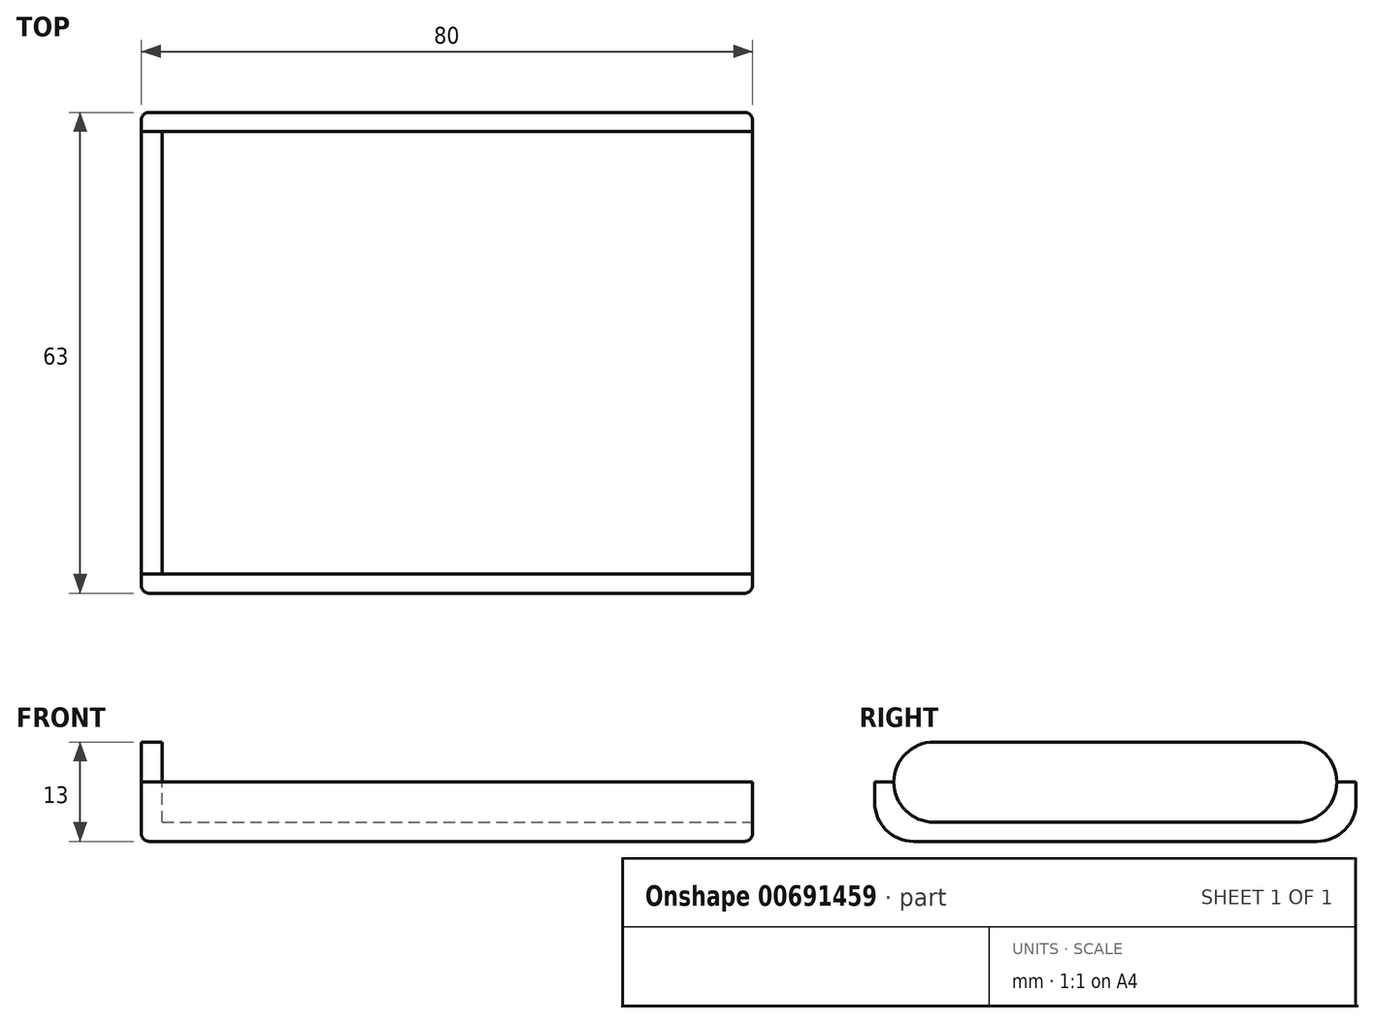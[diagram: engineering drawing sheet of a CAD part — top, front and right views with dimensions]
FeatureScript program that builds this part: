
annotation { "Feature Type Name" : "Feature", "Feature Type Description" : "" }
export const myFeature = defineFeature(function(context is Context, id is Id, definition is map)
    precondition{}
    {
        {
            var Q0;
            Q0=qCreatedBy(makeId("Top.planeOp"),FACE);
            var sketch = newSketch(context, id + "F0", { "sketchPlane" : qUnion([Q0])});
            skLineSegment(sketch, "E0.bottom", {"start": v(-31.63, 23.65) * mm, "end": v(48.37, 23.65) * mm});
            skLineSegment(sketch, "E0.top", {"start": v(-31.63, -39.35) * mm, "end": v(48.37, -39.35) * mm});
            skLineSegment(sketch, "E0.left", {"start": v(-31.63, 23.65) * mm, "end": v(-31.63, -39.35) * mm});
            skLineSegment(sketch, "E0.right", {"start": v(48.37, 23.65) * mm, "end": v(48.37, -39.35) * mm});
            skSolve(sketch);
        }
        {
            var Q0;
            Q0=makeQuery(id+"F0.imprint","IMPRINT",FACE,{"disambiguationData":[TD([[makeQuery(id+"F0.imprint","IMPRINT",EDGE,{"derivedFrom":sQuery(id+"F0.wireOp",EDGE,"E0.bottom")}),-1.0]])]});
            extrude(context, id + "F1", {"entities" : qUnion([Q0]), "depth" : 15.5 * mm, "offsetDistance" : 25.4 * mm});
        }
        {
            var Q0;
            Q0=makeQuery(id+"F1.opExtrude","SWEPT_FACE",FACE,{"disambiguationData":[OSD([sQuery(id+"F0.wireOp",EDGE,"E0.right")])]});
            var sketch = newSketch(context, id + "F2", { "sketchPlane" : qUnion([Q0])});
            skLineSegment(sketch, "E1", {"start": v(-7.85, 2.5) * mm, "end": v(15.9, 2.5) * mm});
            skLineSegment(sketch, "E2", {"start": v(-7.85, 13) * mm, "end": v(15.9, 13) * mm});
            skLineSegment(sketch, "E3", {"start": v(21.15, 7.75) * mm, "end": v(21.15, 7.75) * mm});
            skLineSegment(sketch, "E4", {"start": v(-7.85, 13) * mm, "end": v(-31.6, 13) * mm});
            skLineSegment(sketch, "E5", {"start": v(-7.85, 2.5) * mm, "end": v(-31.6, 2.5) * mm});
            skLineSegment(sketch, "E6", {"start": v(-36.85, 7.75) * mm, "end": v(-36.85, 7.75) * mm});
            skPoint(sketch, "E7.visualSharp", {"position": v(-36.85, 13) * mm});
            skArc(sketch, "E7.filletArc", {"start": v(-31.6, 13) * mm, "mid": v(-35.3, 11.46) * mm, "end": v(-36.85, 7.75) * mm});
            skPoint(sketch, "E8.visualSharp", {"position": v(-36.85, 2.5) * mm});
            skArc(sketch, "E8.filletArc", {"start": v(-36.85, 7.75) * mm, "mid": v(-35.3, 4.04) * mm, "end": v(-31.6, 2.5) * mm});
            skPoint(sketch, "E9.visualSharp", {"position": v(21.15, 13) * mm});
            skArc(sketch, "E9.filletArc", {"start": v(21.15, 7.75) * mm, "mid": v(19.62, 11.46) * mm, "end": v(15.9, 13) * mm});
            skPoint(sketch, "E10.visualSharp", {"position": v(21.15, 2.5) * mm});
            skArc(sketch, "E10.filletArc", {"start": v(15.9, 2.5) * mm, "mid": v(19.62, 4.04) * mm, "end": v(21.15, 7.75) * mm});
            skLineSegment(sketch, "E11", {"start": v(21.15, 7.75) * mm, "end": v(23.65, 7.75) * mm});
            skLineSegment(sketch, "E12", {"start": v(-36.85, 7.75) * mm, "end": v(-39.35, 7.75) * mm});
            skSolve(sketch);
        }
        {
            var Q0;
            Q0=makeQuery(id+"F2.imprint","IMPRINT",FACE,{"disambiguationData":[TD([[makeQuery(id+"F2.imprint","IMPRINT",EDGE,{"derivedFrom":sQuery(id+"F2.wireOp",EDGE,"E1")}),1.0]])]});
            extrude(context, id + "F3", {"entities" : qUnion([Q0]), "operationType" : NewBodyOperationType.REMOVE, "oppositeDirection" : true, "depth" : 77.25 * mm, "offsetDistance" : 25.4 * mm});
        }
        {
            var Q0;
            Q0=makeQuery(id+"F1.opExtrude","CAP_EDGE",EDGE,{"disambiguationData":[OSD([sQuery(id+"F0.wireOp",EDGE,"E0.top")])],"isStart":false});
            var Q1;
            Q1=makeQuery(id+"F1.opExtrude","CAP_EDGE",EDGE,{"disambiguationData":[OSD([sQuery(id+"F0.wireOp",EDGE,"E0.top")])],"isStart":true});
            var Q2;
            Q2=makeQuery(id+"F1.opExtrude","CAP_EDGE",EDGE,{"disambiguationData":[OSD([sQuery(id+"F0.wireOp",EDGE,"E0.bottom")])],"isStart":false});
            var Q3;
            Q3=makeQuery(id+"F1.opExtrude","CAP_EDGE",EDGE,{"disambiguationData":[OSD([sQuery(id+"F0.wireOp",EDGE,"E0.bottom")])],"isStart":true});
            fillet(context, id + "F4", {"entities" : qUnion([Q0, Q1, Q2, Q3]), "radius" : 5.08 * mm, "tangentPropagation" : true, "allowEdgeOverflow" : false});
        }
        {
            var Q0;
            Q0=makeQuery(id+"F1.opExtrude","CAP_EDGE",EDGE,{"disambiguationData":[OSD([sQuery(id+"F0.wireOp",EDGE,"E0.left")])],"isStart":false});
            var Q1;
            Q1=makeQuery(id+"F1.opExtrude","CAP_EDGE",EDGE,{"disambiguationData":[OSD([sQuery(id+"F0.wireOp",EDGE,"E0.right")])],"isStart":false});
            fillet(context, id + "F5", {"entities" : qUnion([Q0, Q1]), "radius" : 1 * mm, "tangentPropagation" : true, "allowEdgeOverflow" : false});
        }
        {
            var Q0;
            Q0=makeQuery(id+"F2.imprint","IMPRINT",FACE,{"disambiguationData":[TD([[makeQuery(id+"F2.imprint","IMPRINT",EDGE,{"derivedFrom":sQuery(id+"F2.wireOp",EDGE,"E2")}),1.0]])]});
            extrude(context, id + "F6", {"entities" : qUnion([Q0]), "operationType" : NewBodyOperationType.REMOVE, "oppositeDirection" : true, "depth" : 98.55 * mm, "offsetDistance" : 25.4 * mm});
        }
    });
